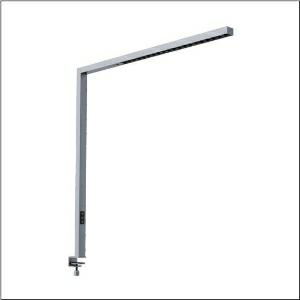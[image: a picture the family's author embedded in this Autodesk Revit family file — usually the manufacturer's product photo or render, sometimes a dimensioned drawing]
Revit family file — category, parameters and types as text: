
# Revit family: silica_r__31_desk_51my52gatcs_8ab4
name_source: partatom
category: Lighting Fixtures
units: mm (PartAtom-declared; Revit-internal decimal feet)

## family parameters
Cut with Voids When Loaded = No
Host = Face
Light Source = No
Part Type = Normal
Room Calculation Point = No
Round Connector Dimension = Use Diameter
Shared = No

## types (1)
- --- (1 x LED, 8520 lm, 71 W, 4000K)
    Apparent Load = 71 VA
    CIE Flux Codes = 86 100 100 24 100
    Color Rendering = 80
    Color Temperature = 4000K
    Default Elevation = 1800 mm
    Description = Silica® 31 Desk, desktop luminaire, secondary optical cover: cover panel, of PMMA, light emission: direct/indirect distribution, primary light characteristic: symmetric, installation type: as desk luminaire, LED, rated luminous flux: 8.520lm, luminous efficacy: 120lm/W, light colour: 8tw, colour temperature: 2700..6500K, control gear: Touchdim, daylight-dependent control, with cable with plug, mains connection: 230V, AC, 50Hz, connection cable pre-assembled, rated input power: 71W, luminaire head, of aluminium, metallic grey (RAL 9006), length: 1.203mm, width: 52mm, supporting column, angular, of aluminium, metallic grey (RAL 9006), baseplate, of steel, metallic grey (RAL 9006), protection rating (complete): IP20, insulation class (complete): insulation class I (protective earthing), certification: CE, permissible operating ambient temperature: -20..+40°C, standard: EN 50419, packaging unit: 1 piece
    Height = 36 mm
    Lamp = 1 x LED
    Lamp Light Flux = 8520 lm
    Lamp Power = 71 W
    Lamp count = 1
    Length = 1203 mm
    Luminous efficacy = 120 lm/W
    Manufacturer = Siteco
    ModVariant = No
    Model = 51MY52GATCS
    Mounting Place = Floor
    Mounting Type = Freestanding
    Number of Poles = 1
    OnlyDefault = Yes
    Power Factor = 1
    Product Name = Silica® 31 Desk
    Product group = desktop luminaire
    ProductGroupID = 1303
    Protection Class = Protection class I
    Protection Degree = IP 20
    RLX_Detail_Level = 1
    RLX_Emergency_Light_Flux = 0 lm
    RLX_Emergency_Type = 0
    RLX_Emergency_Type_DB = No
    RlxData = <blob elided: 19617 chars, md5=94abdb09>
    Socket = socket
    Standby Power = 0 W
    System Light Flux = 8520 lm
    System Power = 71 W
    Type Comments = factory setting
    Type Image = l_1275333.jpg
    URL = http://relux.com
    VarID = @adj_080206
    Voltage = 0 V
    Weight = 0.00 kg
    Width = 52 mm  [stored 0.170604 ft]

note: [stored X ft] marks values corroborated as IEEE doubles in the binary element streams (Revit-internal decimal feet)

## geometry (parser evidence)
native form markers: Blend x4, Sweep x15
no freeform markers — native parametric forms only
